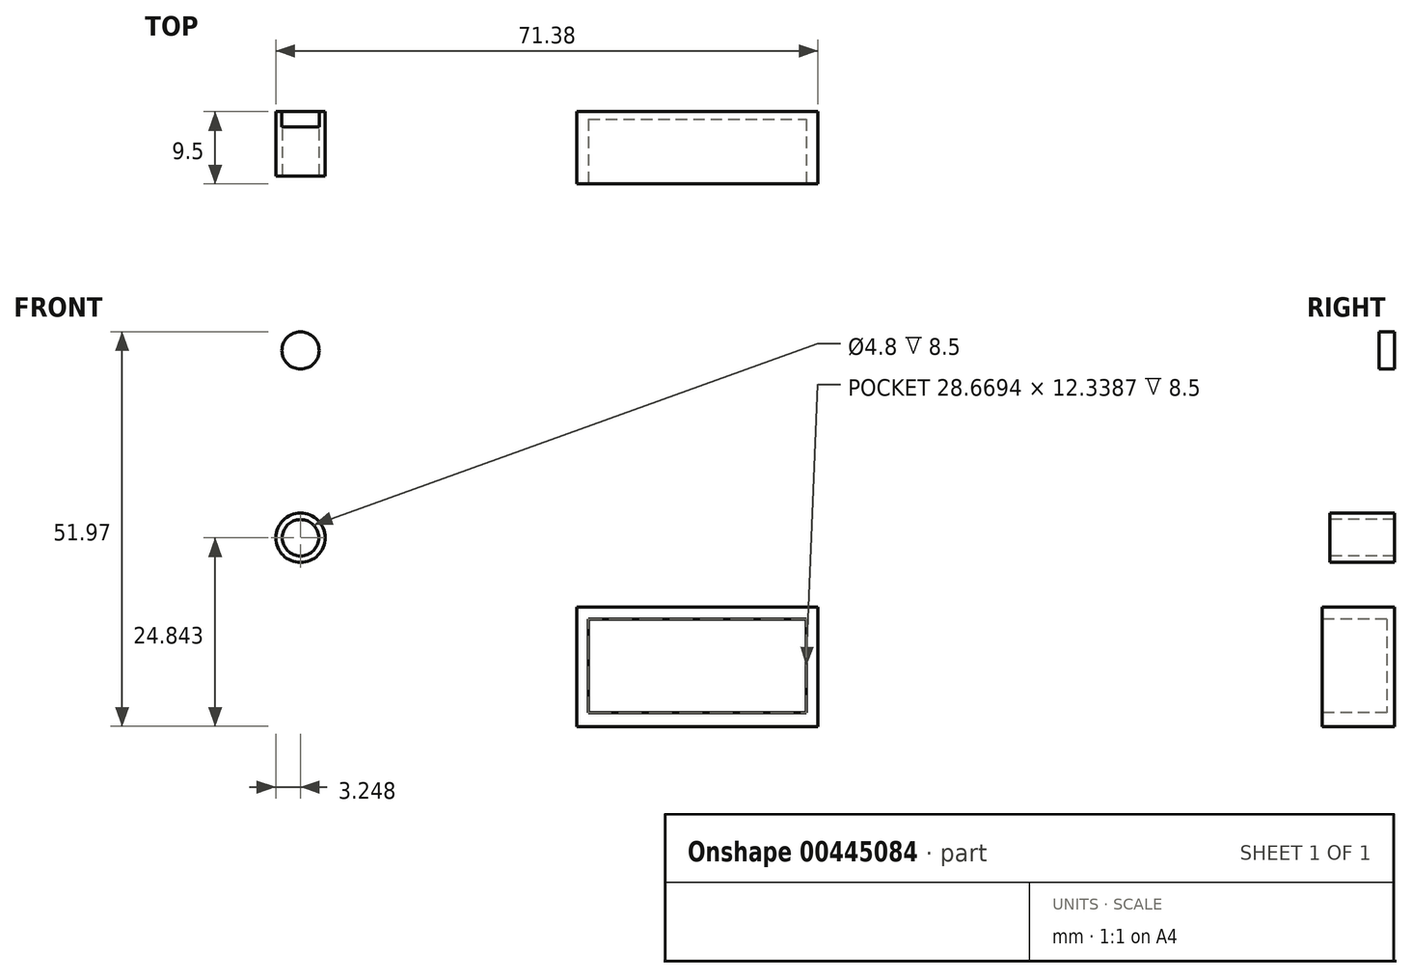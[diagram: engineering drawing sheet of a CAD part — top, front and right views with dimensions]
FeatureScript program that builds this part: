
annotation { "Feature Type Name" : "Feature", "Feature Type Description" : "" }
export const myFeature = defineFeature(function(context is Context, id is Id, definition is map)
    precondition{}
    {
        {
            var Q0;
            Q0=qCreatedBy(makeId("Front.planeOp"),FACE);
            var sketch = newSketch(context, id + "F0", { "sketchPlane" : qUnion([Q0])});
            skLineSegment(sketch, "E0.bottom", {"start": v(-15.15, 3.79) * mm, "end": v(16.6, 3.79) * mm});
            skLineSegment(sketch, "E0.top", {"start": v(-15.15, -11.96) * mm, "end": v(16.6, -11.96) * mm});
            skLineSegment(sketch, "E0.left", {"start": v(-15.15, 3.79) * mm, "end": v(-15.15, -11.96) * mm});
            skLineSegment(sketch, "E0.right", {"start": v(16.6, 3.79) * mm, "end": v(16.6, -11.96) * mm});
            skSolve(sketch);
        }
        {
            var Q0;
            Q0 = qSketchRegion(id + "F0", true);
            extrude(context, id + "F1", {"entities" : qUnion([Q0]), "depth" : 9.5 * mm});
        }
        {
            var Q0;
            Q0=qCreatedBy(makeId("Front.planeOp"),FACE);
            var sketch = newSketch(context, id + "F2", { "sketchPlane" : qUnion([Q0])});
            skCircle(sketch, "E1", {"center": v(-51.53, 37.56) * mm, "radius": 2.45 * mm});
            skSolve(sketch);
        }
        {
            var Q0;
            Q0 = qSketchRegion(id + "F2", true);
            extrude(context, id + "F3", {"entities" : qUnion([Q0]), "depth" : 2 * mm});
        }
        {
            var Q0;
            Q0=makeQuery(id+"F1.opExtrude","CAP_FACE",FACE,{"disambiguationData":[OSD([sQuery(id+"F0.wireOp",EDGE,"E0.bottom"),sQuery(id+"F0.wireOp",EDGE,"E0.top"),sQuery(id+"F0.wireOp",EDGE,"E0.left"),sQuery(id+"F0.wireOp",EDGE,"E0.right")])],"isStart":false});
            var sketch = newSketch(context, id + "F4", { "sketchPlane" : qUnion([Q0])});
            skLineSegment(sketch, "E2.bottom", {"start": v(-13.6, 2.18) * mm, "end": v(15.06, 2.18) * mm});
            skLineSegment(sketch, "E2.top", {"start": v(-13.6, -10.16) * mm, "end": v(15.06, -10.16) * mm});
            skLineSegment(sketch, "E2.left", {"start": v(-13.6, 2.18) * mm, "end": v(-13.6, -10.16) * mm});
            skLineSegment(sketch, "E2.right", {"start": v(15.06, 2.18) * mm, "end": v(15.06, -10.16) * mm});
            skSolve(sketch);
        }
        {
            var Q0;
            Q0=makeQuery(id+"F4.imprint","IMPRINT",FACE,{"disambiguationData":[TD([[makeQuery(id+"F4.imprint","IMPRINT",EDGE,{"derivedFrom":sQuery(id+"F4.wireOp",EDGE,"E2.bottom")}),-1.0]])]});
            extrude(context, id + "F5", {"entities" : qUnion([Q0]), "operationType" : NewBodyOperationType.REMOVE, "oppositeDirection" : true, "depth" : 8.5 * mm});
        }
        {
            var Q0;
            Q0=qCreatedBy(makeId("Front.planeOp"),FACE);
            var sketch = newSketch(context, id + "F6", { "sketchPlane" : qUnion([Q0])});
            skCircle(sketch, "E3", {"center": v(-51.53, 12.88) * mm, "radius": 3.25 * mm});
            skSolve(sketch);
        }
        {
            var Q0;
            Q0 = qSketchRegion(id + "F6", true);
            extrude(context, id + "F7", {"entities" : qUnion([Q0]), "depth" : 8.5 * mm});
        }
        {
            var Q0;
            Q0=makeQuery(id+"F7.opExtrude","CAP_FACE",FACE,{"disambiguationData":[OSD([sQuery(id+"F6.wireOp",EDGE,"E3")])],"isStart":false});
            var sketch = newSketch(context, id + "F8", { "sketchPlane" : qUnion([Q0])});
            skCircle(sketch, "E4", {"center": v(-51.53, 12.88) * mm, "radius": 2.4 * mm});
            skSolve(sketch);
        }
        {
            var Q0;
            Q0=makeQuery(id+"F8.imprint","IMPRINT",FACE,{"disambiguationData":[TD([[makeQuery(id+"F8.imprint","IMPRINT",EDGE,{"derivedFrom":sQuery(id+"F8.wireOp",EDGE,"E4")}),1.0]])]});
            extrude(context, id + "F9", {"entities" : qUnion([Q0]), "operationType" : NewBodyOperationType.REMOVE, "oppositeDirection" : true, "depth" : 8.5 * mm});
        }
    });
